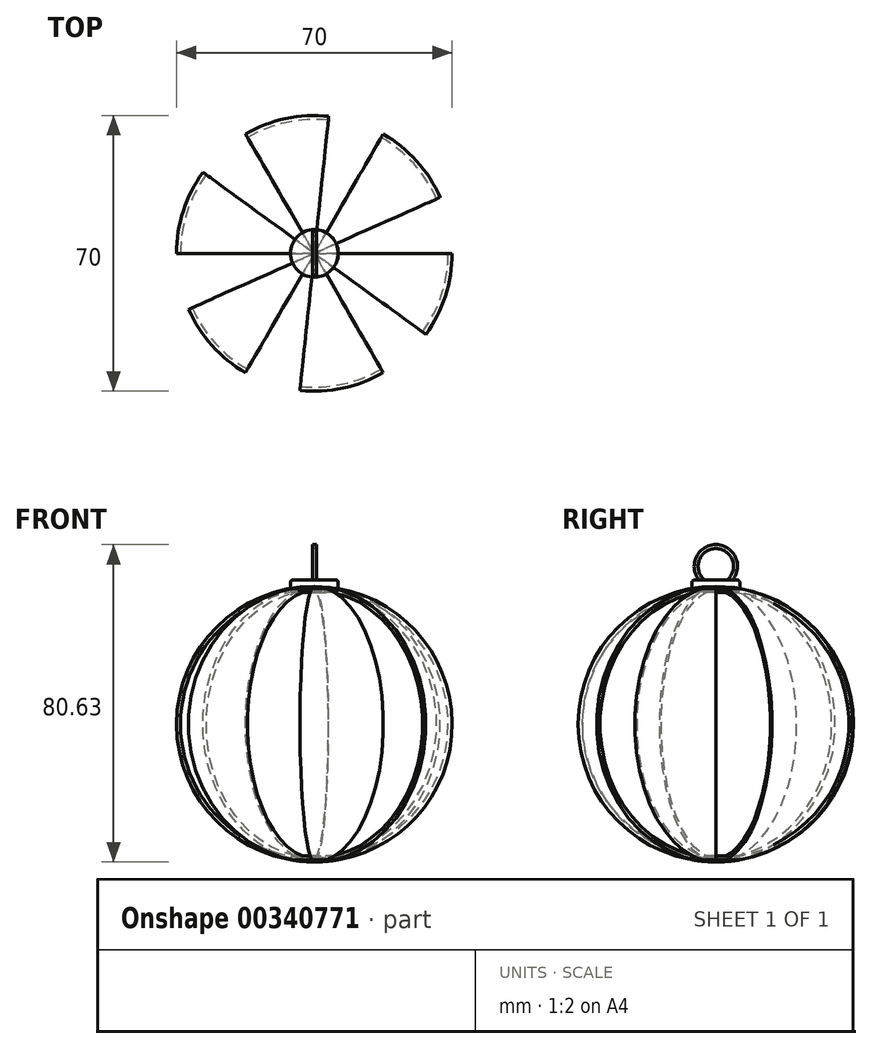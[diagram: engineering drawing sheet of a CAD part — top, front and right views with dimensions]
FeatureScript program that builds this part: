
annotation { "Feature Type Name" : "Feature", "Feature Type Description" : "" }
export const myFeature = defineFeature(function(context is Context, id is Id, definition is map)
    precondition{}
    {
        {
            var Q0;
            Q0=qCreatedBy(makeId("Front.planeOp"),FACE);
            var sketch = newSketch(context, id + "F0", { "sketchPlane" : qUnion([Q0])});
            skLineSegment(sketch, "E0", {"start": v(0, 104.83) * mm, "end": v(0, -73.87) * mm, "construction": true});
            skArc(sketch, "E1", {"start": v(0, -35) * mm, "mid": v(35, 0) * mm, "end": v(0, 35) * mm});
            skArc(sketch, "E2.0", {"start": v(0, -34) * mm, "mid": v(34, 0) * mm, "end": v(0, 34) * mm});
            skLineSegment(sketch, "E3", {"start": v(0, 35) * mm, "end": v(0, 34) * mm});
            skLineSegment(sketch, "E4", {"start": v(0, -35) * mm, "end": v(0, -34) * mm});
            skSolve(sketch);
        }
        {
            var Q0;
            Q0=makeQuery(id+"F0.imprint","IMPRINT",FACE,{"disambiguationData":[TD([[makeQuery(id+"F0.imprint","IMPRINT",EDGE,{"derivedFrom":sQuery(id+"F0.wireOp",EDGE,"E1")}),1.0]])]});
            var Q1;
            Q1=sQuery(id+"F0.wireOp",EDGE,"E0");
            revolve(context, id + "F1", {"entities" : qUnion([Q0]), "axis" : qUnion([Q1]), "revolveType" : RevolveType.ONE_DIRECTION, "angle" : 36 * degree});
        }
        {
            var Q0;
            Q0=qCreatedBy(makeId("Front.planeOp"),FACE);
            var sketch = newSketch(context, id + "F2", { "sketchPlane" : qUnion([Q0])});
            skLineSegment(sketch, "E5", {"start": v(0, 73.22) * mm, "end": v(0, -54.95) * mm, "construction": true});
            skSolve(sketch);
        }
        {
            var Q0;
            Q0=makeQuery(id+"F1.opRevolve","SWEPT_BODY",BODY,{"disambiguationData":[OSD([sQuery(id+"F0.wireOp",EDGE,"E1"),sQuery(id+"F0.wireOp",EDGE,"E2.0"),sQuery(id+"F0.wireOp",EDGE,"E3"),sQuery(id+"F0.wireOp",EDGE,"E4")])]});
            var Q1;
            Q1=sQuery(id+"F2.wireOp",EDGE,"E5");
            circularPattern(context, id + "F3", {"entities" : qUnion([Q0]), "axis" : qUnion([Q1]), "angle" : 360 * degree, "instanceCount" : 6, "equalSpace" : true});
        }
        {
            var Q0;
            Q0=qCreatedBy(makeId("Right.planeOp"),FACE);
            var sketch = newSketch(context, id + "F4", { "sketchPlane" : qUnion([Q0])});
            skArc(sketch, "E6", {"start": v(6.08, 34.47) * mm, "mid": v(3.05, 34.87) * mm, "end": v(0, 35) * mm});
            skArc(sketch, "E7", {"start": v(5.9, 33.48) * mm, "mid": v(2.96, 33.87) * mm, "end": v(0, 34) * mm});
            skLineSegment(sketch, "E8", {"start": v(0, 0) * mm, "end": v(9.07, 51.41) * mm, "construction": true});
            skLineSegment(sketch, "E9", {"start": v(6.08, 34.47) * mm, "end": v(5.9, 33.48) * mm});
            skLineSegment(sketch, "E10", {"start": v(0, 35) * mm, "end": v(0, 34) * mm});
            skLineSegment(sketch, "E11", {"start": v(0, -43.64) * mm, "end": v(0, 69.85) * mm, "construction": true});
            skLineSegment(sketch, "E12.MirrorCS", {"start": v(6.08, -34.47) * mm, "end": v(5.9, -33.48) * mm});
            skLineSegment(sketch, "E13.MirrorCS", {"start": v(0, -35) * mm, "end": v(0, -34) * mm});
            skArc(sketch, "E14.MirrorCS", {"start": v(6.08, -34.47) * mm, "mid": v(3.05, -34.87) * mm, "end": v(0, -35) * mm});
            skArc(sketch, "E15.MirrorCS", {"start": v(5.9, -33.48) * mm, "mid": v(2.96, -33.87) * mm, "end": v(0, -34) * mm});
            skSolve(sketch);
        }
        {
            var Q0;
            Q0 = qSketchRegion(id + "F4", true);
            var Q1;
            Q1=sQuery(id+"F4.wireOp",EDGE,"E11");
            revolve(context, id + "F5", {"entities" : qUnion([Q0]), "axis" : qUnion([Q1]), "revolveType" : RevolveType.FULL});
        }
        {
            var Q0;
            Q0=qCreatedBy(makeId("Right.planeOp"),FACE);
            var sketch = newSketch(context, id + "F6", { "sketchPlane" : qUnion([Q0])});
            skLineSegment(sketch, "E16", {"start": v(0, 33.98) * mm, "end": v(-6.06, 33.98) * mm});
            skLineSegment(sketch, "E17", {"start": v(-6.06, 33.98) * mm, "end": v(-6.06, 35.98) * mm});
            skLineSegment(sketch, "E18", {"start": v(-5.36, 36.68) * mm, "end": v(0, 36.68) * mm});
            skPoint(sketch, "E19.visualSharp", {"position": v(-6.06, 36.68) * mm});
            skArc(sketch, "E19.filletArc", {"start": v(-5.36, 36.68) * mm, "mid": v(-5.86, 36.48) * mm, "end": v(-6.06, 35.98) * mm});
            skLineSegment(sketch, "E20", {"start": v(0, 41.3) * mm, "end": v(0, 33.98) * mm});
            skLineSegment(sketch, "E21", {"start": v(0, 63.23) * mm, "end": v(0, 9.23) * mm, "construction": true});
            skLineSegment(sketch, "E22", {"start": v(0, 36.68) * mm, "end": v(0, 33.98) * mm});
            skSolve(sketch);
        }
        {
            var Q0;
            Q0 = qSketchRegion(id + "F6", true);
            var Q1;
            Q1=sQuery(id+"F6.wireOp",EDGE,"E21");
            revolve(context, id + "F7", {"entities" : qUnion([Q0]), "axis" : qUnion([Q1]), "revolveType" : RevolveType.FULL});
        }
        {
            var Q0;
            Q0=qCreatedBy(makeId("Right.planeOp"),FACE);
            var sketch = newSketch(context, id + "F8", { "sketchPlane" : qUnion([Q0])});
            skArc(sketch, "E23", {"start": v(4.29, 36.68) * mm, "mid": v(0, 45.63) * mm, "end": v(-4.29, 36.68) * mm});
            skArc(sketch, "E24", {"start": v(2.9, 36.68) * mm, "mid": v(0, 44.63) * mm, "end": v(-2.9, 36.68) * mm});
            skLineSegment(sketch, "E25", {"start": v(-5.53, 36.68) * mm, "end": v(9.47, 36.68) * mm, "construction": true});
            skLineSegment(sketch, "E26", {"start": v(-4.29, 36.68) * mm, "end": v(-2.9, 36.68) * mm});
            skLineSegment(sketch, "E27", {"start": v(2.9, 36.68) * mm, "end": v(4.29, 36.68) * mm});
            skSolve(sketch);
        }
        {
            var Q0;
            Q0 = qSketchRegion(id + "F8", true);
            extrude(context, id + "F9", {"entities" : qUnion([Q0]), "operationType" : NewBodyOperationType.ADD, "endBound" : BoundingType.SYMMETRIC, "depth" : 1 * mm});
        }
    });
